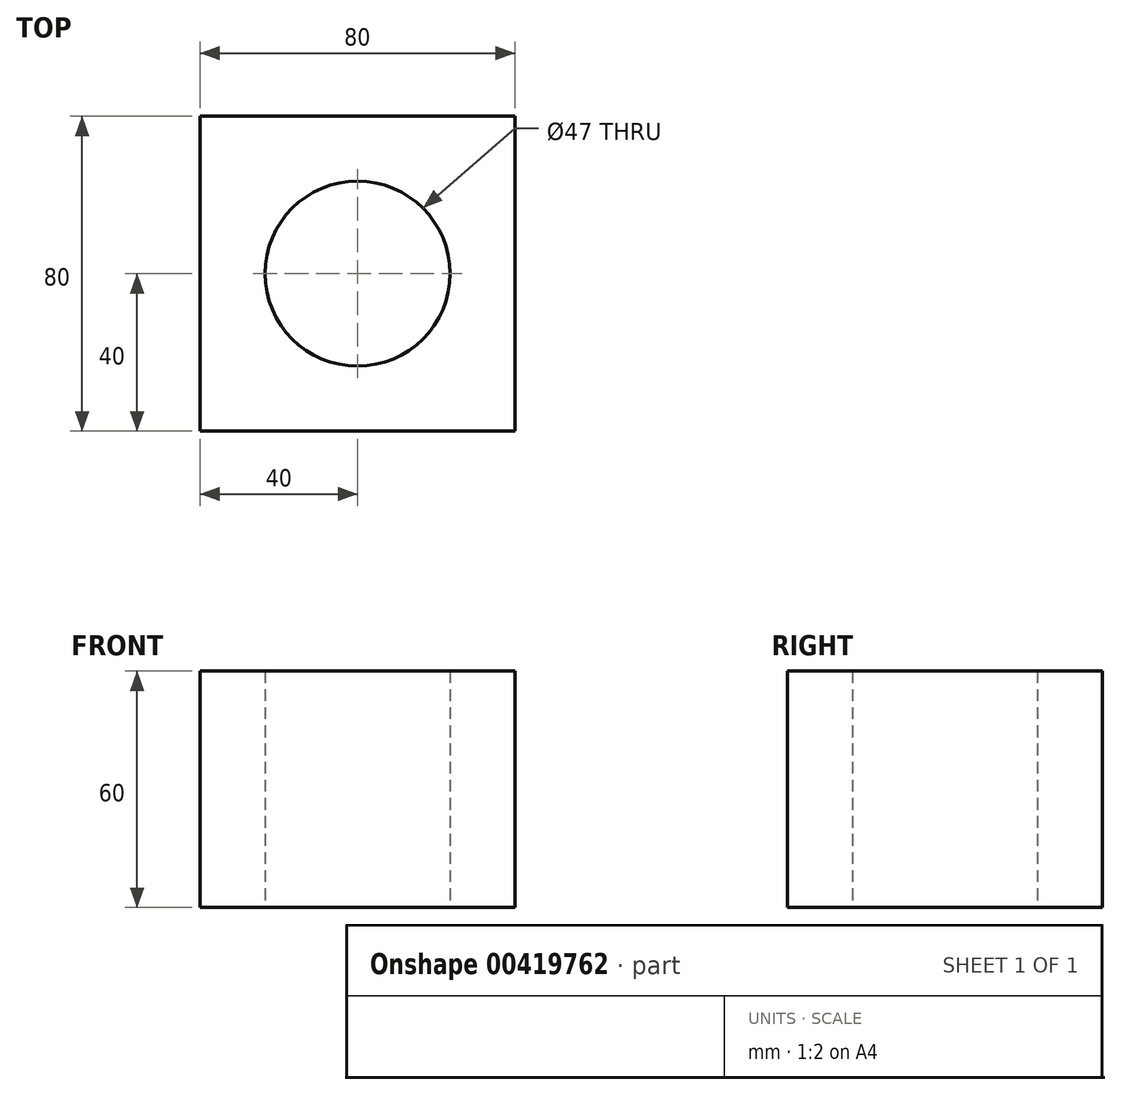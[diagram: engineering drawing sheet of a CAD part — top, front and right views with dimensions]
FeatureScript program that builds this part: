
annotation { "Feature Type Name" : "Feature", "Feature Type Description" : "" }
export const myFeature = defineFeature(function(context is Context, id is Id, definition is map)
    precondition{}
    {
        {
            var Q0;
            Q0=qCreatedBy(makeId("Top.planeOp"),FACE);
            var sketch = newSketch(context, id + "F0", { "sketchPlane" : qUnion([Q0])});
            skCircle(sketch, "E0", {"center": v(0, 0) * mm, "radius": 23.5 * mm});
            skLineSegment(sketch, "E1.bottom", {"start": v(-40, 40) * mm, "end": v(40, 40) * mm});
            skLineSegment(sketch, "E1.top", {"start": v(-40, -40) * mm, "end": v(40, -40) * mm});
            skLineSegment(sketch, "E1.left", {"start": v(-40, 40) * mm, "end": v(-40, -40) * mm});
            skLineSegment(sketch, "E1.right", {"start": v(40, 40) * mm, "end": v(40, -40) * mm});
            skSolve(sketch);
        }
        {
            var Q0;
            Q0=makeQuery(id+"F0.imprint","IMPRINT",FACE,{"disambiguationData":[TD([[makeQuery(id+"F0.imprint","IMPRINT",EDGE,{"derivedFrom":sQuery(id+"F0.wireOp",EDGE,"E0")}),-1.0]])]});
            extrude(context, id + "F1", {"entities" : qUnion([Q0]), "depth" : 40 * mm, "offsetDistance" : 25 * mm, "hasSecondDirection" : true, "secondDirectionOppositeDirection" : true, "secondDirectionDepth" : 20 * mm});
        }
    });
